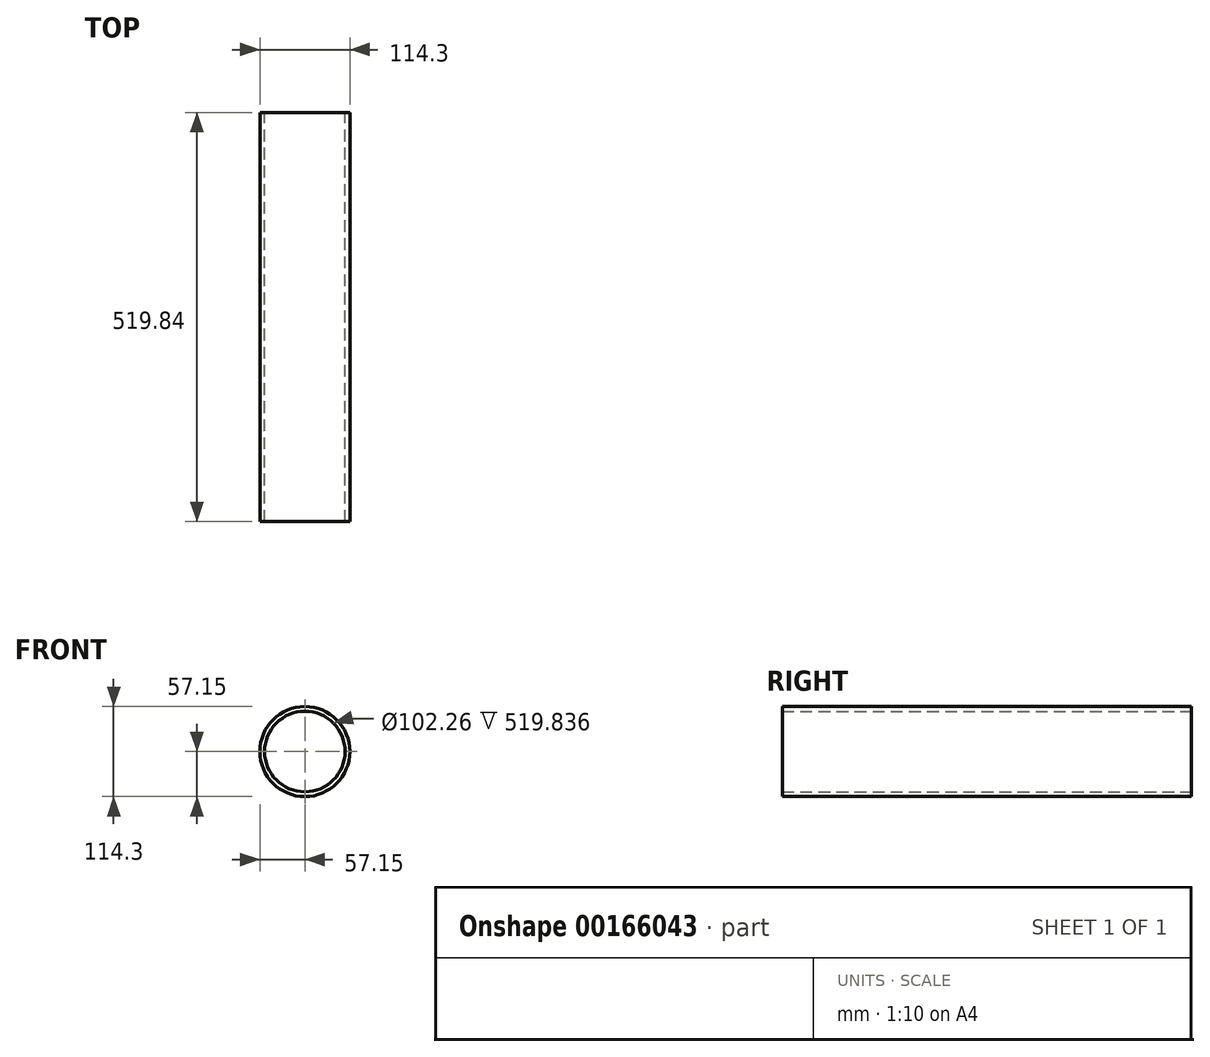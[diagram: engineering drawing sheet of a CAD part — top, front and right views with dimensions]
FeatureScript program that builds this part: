
annotation { "Feature Type Name" : "Feature", "Feature Type Description" : "" }
export const myFeature = defineFeature(function(context is Context, id is Id, definition is map)
    precondition{}
    {
        {
            var Q0;
            Q0=qCreatedBy(makeId("Front.planeOp"),FACE);
            var sketch = newSketch(context, id + "F0", { "sketchPlane" : qUnion([Q0])});
            skCircle(sketch, "E0", {"center": v(0, 0) * mm, "radius": 51.13 * mm});
            skCircle(sketch, "E1", {"center": v(0, 0) * mm, "radius": 57.15 * mm});
            skSolve(sketch);
        }
        {
            var Q0;
            Q0=makeQuery(id+"F0.imprint","IMPRINT",FACE,{"disambiguationData":[TD([[makeQuery(id+"F0.imprint","IMPRINT",EDGE,{"derivedFrom":sQuery(id+"F0.wireOp",EDGE,"E0")}),-1.0]])]});
            extrude(context, id + "F1", {"entities" : qUnion([Q0]), "endBound" : BoundingType.SYMMETRIC, "depth" : 519.84 * mm});
        }
    });
